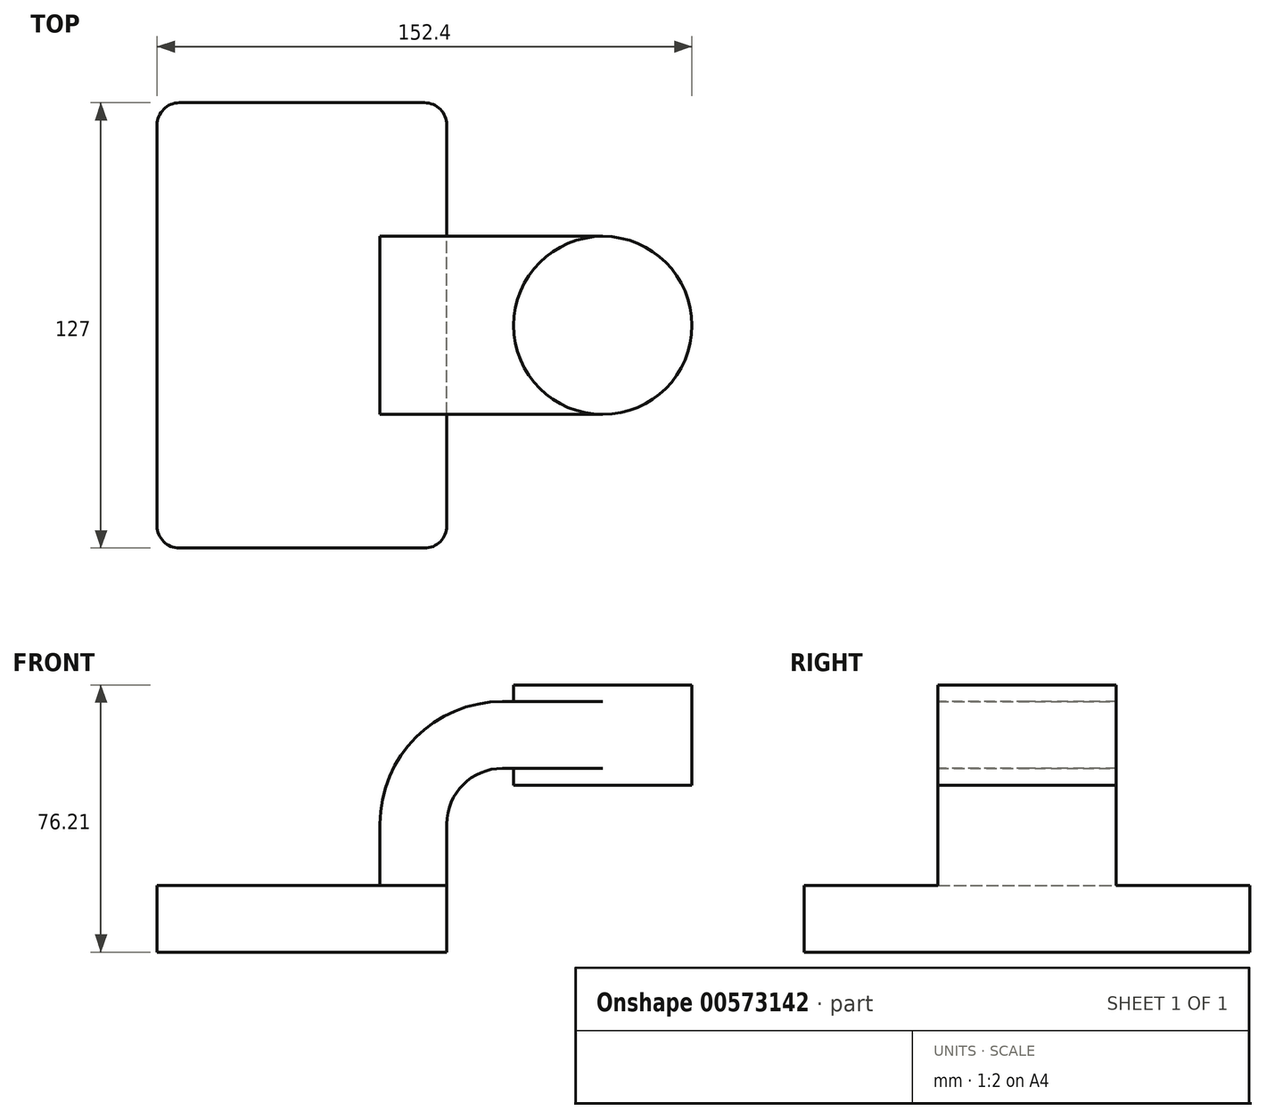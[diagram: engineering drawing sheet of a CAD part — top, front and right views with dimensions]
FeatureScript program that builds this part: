
annotation { "Feature Type Name" : "Feature", "Feature Type Description" : "" }
export const myFeature = defineFeature(function(context is Context, id is Id, definition is map)
    precondition{}
    {
        {
            var Q0;
            Q0=qCreatedBy(makeId("Front.planeOp"),FACE);
            var sketch = newSketch(context, id + "F0", { "sketchPlane" : qUnion([Q0])});
            skLineSegment(sketch, "E0.bottom", {"start": v(-41.27, 9.53) * mm, "end": v(41.28, 9.53) * mm});
            skLineSegment(sketch, "E0.top", {"start": v(-41.28, -9.52) * mm, "end": v(41.27, -9.52) * mm});
            skLineSegment(sketch, "E0.left", {"start": v(-41.28, 9.53) * mm, "end": v(-41.28, -9.52) * mm});
            skLineSegment(sketch, "E0.right", {"start": v(41.28, 9.53) * mm, "end": v(41.27, -9.52) * mm});
            skPoint(sketch, "E0.middle", {"position": v(0, 0) * mm});
            skLineSegment(sketch, "E1.bottom", {"start": v(111.12, 66.68) * mm, "end": v(60.32, 66.68) * mm});
            skLineSegment(sketch, "E1.top", {"start": v(111.12, 38.1) * mm, "end": v(60.33, 38.1) * mm});
            skLineSegment(sketch, "E1.left", {"start": v(111.12, 66.68) * mm, "end": v(111.13, 38.1) * mm});
            skLineSegment(sketch, "E1.right", {"start": v(60.32, 66.68) * mm, "end": v(60.33, 38.1) * mm});
            skPoint(sketch, "E1.middle", {"position": v(85.72, 52.39) * mm});
            skLineSegment(sketch, "E2", {"start": v(41.28, 9.52) * mm, "end": v(41.28, 27) * mm});
            skArc(sketch, "E3", {"start": v(41.27, 27) * mm, "mid": v(45.92, 38.23) * mm, "end": v(57.15, 42.88) * mm});
            skLineSegment(sketch, "E4", {"start": v(57.15, 42.88) * mm, "end": v(85.72, 42.88) * mm});
            skLineSegment(sketch, "E5.0", {"start": v(57.15, 61.93) * mm, "end": v(85.72, 61.93) * mm});
            skArc(sketch, "E5.1", {"start": v(22.23, 27) * mm, "mid": v(32.45, 51.7) * mm, "end": v(57.15, 61.93) * mm});
            skLineSegment(sketch, "E5.2", {"start": v(22.23, 9.52) * mm, "end": v(22.23, 27) * mm});
            skLineSegment(sketch, "E6", {"start": v(85.72, 38.1) * mm, "end": v(85.72, 66.68) * mm});
            skFitSpline(sketch, "E7", {"points": [v(-41.28, 9.52) * mm, v(57.15, 61.93) * mm], "startDerivative": vector(0.6, 116.1) * mm, "endDerivative": vector(114.75, -1.66) * mm});
            skSolve(sketch);
        }
        {
            var Q0;
            Q0=makeQuery(id+"F0.imprint","IMPRINT",FACE,{"disambiguationData":[TD([[makeQuery(id+"F0.imprint","IMPRINT",EDGE,{"derivedFrom":sQuery(id+"F0.wireOp",EDGE,"E0.top")}),1.0]])]});
            extrude(context, id + "F1", {"entities" : qUnion([Q0]), "endBound" : BoundingType.SYMMETRIC, "depth" : 127 * mm, "offsetDistance" : 25.4 * mm});
        }
        {
            var Q0;
            {var subQ1=sQuery(id+"F0.wireOp",EDGE,"E2");Q0=makeQuery(id+"F0.imprint","IMPRINT",FACE,{"disambiguationData":[TD([[makeQuery(id+"F0.imprint","IMPRINT",EDGE,{"derivedFrom":subQ1}),1.0]])]});}
            var Q1;
            {var subQ0=sQuery(id+"F0.wireOp",EDGE,"E5.0");var subQ1=sQuery(id+"F0.wireOp",EDGE,"E1.right");var subQ2=makeQuery(id+"F0.imprint","INTERSECT",VERTEX,{"derivedFrom":[subQ1,subQ0]});Q1=makeQuery(id+"F0.imprint","IMPRINT",FACE,{"disambiguationData":[TD([[makeQuery(id+"F0.imprint","IMPRINT",EDGE,{"disambiguationData":[TD([[subQ2,-1.0]])],"derivedFrom":subQ1}),1.0]])]});}
            extrude(context, id + "F2", {"entities" : qUnion([Q0, Q1]), "operationType" : NewBodyOperationType.ADD, "endBound" : BoundingType.SYMMETRIC, "depth" : 50.8 * mm, "offsetDistance" : 25.4 * mm});
        }
        {
            var Q0;
            Q0=makeQuery(id+"F0.imprint","IMPRINT",FACE,{"disambiguationData":[TD([[makeQuery(id+"F0.imprint","IMPRINT",EDGE,{"derivedFrom":sQuery(id+"F0.wireOp",EDGE,"E5.1")}),1.0]])]});
            extrude(context, id + "F3", {"entities" : qUnion([Q0]), "operationType" : NewBodyOperationType.ADD, "endBound" : BoundingType.SYMMETRIC, "depth" : 15.88 * mm, "offsetDistance" : 25.4 * mm});
        }
        {
            var Q0;
            {var subQ4=sQuery(id+"F0.wireOp",EDGE,"E1.left");Q0=makeQuery(id+"F0.imprint","IMPRINT",FACE,{"disambiguationData":[TD([[makeQuery(id+"F0.imprint","IMPRINT",EDGE,{"derivedFrom":subQ4}),-1.0]])]});}
            var Q1;
            Q1=sQuery(id+"F0.wireOp",EDGE,"E6");
            revolve(context, id + "F4", {"operationType" : NewBodyOperationType.ADD, "entities" : qUnion([Q0]), "axis" : qUnion([Q1]), "revolveType" : RevolveType.FULL});
        }
        {
            var Q0;
            Q0=makeQuery(id+"F1.opExtrude","CAP_EDGE",EDGE,{"disambiguationData":[OSD([sQuery(id+"F0.wireOp",EDGE,"E0.right")])],"isStart":false});
            var Q1;
            Q1=makeQuery(id+"F1.opExtrude","CAP_EDGE",EDGE,{"disambiguationData":[OSD([sQuery(id+"F0.wireOp",EDGE,"E0.left")])],"isStart":false});
            var Q2;
            Q2=makeQuery(id+"F1.opExtrude","CAP_EDGE",EDGE,{"disambiguationData":[OSD([sQuery(id+"F0.wireOp",EDGE,"E0.right")])],"isStart":true});
            var Q3;
            Q3=makeQuery(id+"F1.opExtrude","CAP_EDGE",EDGE,{"disambiguationData":[OSD([sQuery(id+"F0.wireOp",EDGE,"E0.left")])],"isStart":true});
            fillet(context, id + "F5", {"entities" : qUnion([Q0, Q1, Q2, Q3]), "radius" : 6.35 * mm, "tangentPropagation" : true, "allowEdgeOverflow" : false});
        }
    });
